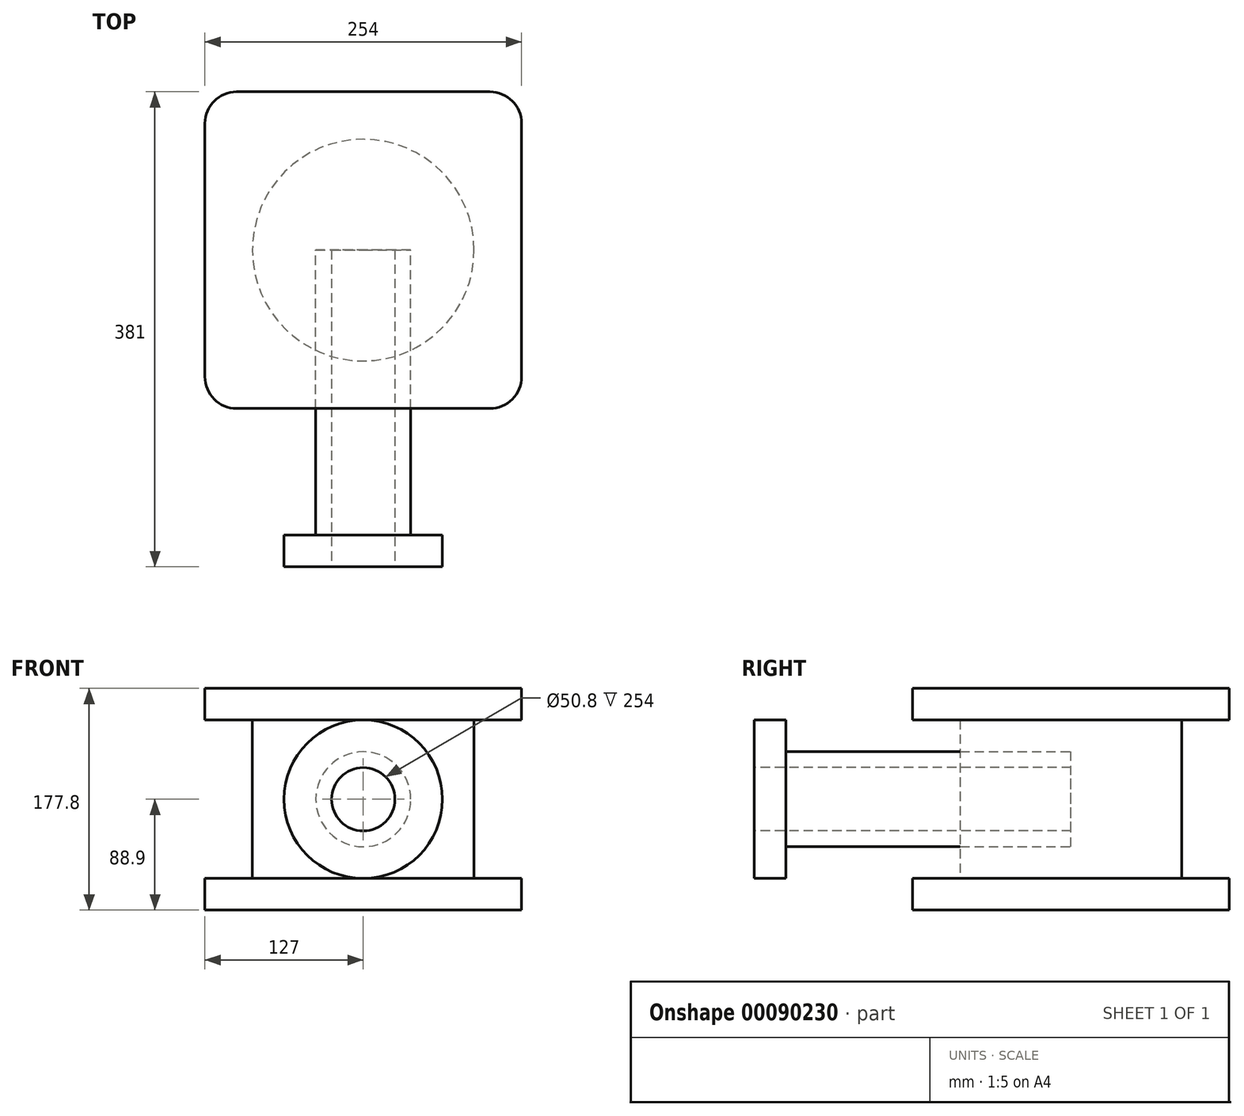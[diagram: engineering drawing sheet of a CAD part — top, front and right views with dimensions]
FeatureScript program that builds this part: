
annotation { "Feature Type Name" : "Feature", "Feature Type Description" : "" }
export const myFeature = defineFeature(function(context is Context, id is Id, definition is map)
    precondition{}
    {
        {
            var Q0;
            Q0=qCreatedBy(makeId("Top.planeOp"),FACE);
            var sketch = newSketch(context, id + "F0", { "sketchPlane" : qUnion([Q0])});
            skLineSegment(sketch, "E0", {"start": v(0, 127) * mm, "end": v(101.6, 127) * mm});
            skLineSegment(sketch, "E1", {"start": v(127, 101.6) * mm, "end": v(127, 0) * mm});
            skLineSegment(sketch, "E2.MirrorCS", {"start": v(0, 127) * mm, "end": v(-101.6, 127) * mm});
            skLineSegment(sketch, "E3.MirrorCS", {"start": v(-127, 101.6) * mm, "end": v(-127, 0) * mm});
            skLineSegment(sketch, "E4.MirrorCS", {"start": v(-127, -101.6) * mm, "end": v(-127, 0) * mm});
            skLineSegment(sketch, "E5.MirrorCS", {"start": v(0, -127) * mm, "end": v(-101.6, -127) * mm});
            skLineSegment(sketch, "E6.MirrorCS", {"start": v(0, -127) * mm, "end": v(101.6, -127) * mm});
            skLineSegment(sketch, "E7.MirrorCS", {"start": v(127, -101.6) * mm, "end": v(127, 0) * mm});
            skPoint(sketch, "E8.visualSharp", {"position": v(-127, 127) * mm});
            skArc(sketch, "E8.filletArc", {"start": v(-101.6, 127) * mm, "mid": v(-119.56, 119.56) * mm, "end": v(-127, 101.6) * mm});
            skPoint(sketch, "E9.visualSharp", {"position": v(127, 127) * mm});
            skArc(sketch, "E9.filletArc", {"start": v(127, 101.6) * mm, "mid": v(119.56, 119.56) * mm, "end": v(101.6, 127) * mm});
            skPoint(sketch, "E10.visualSharp", {"position": v(127, -127) * mm});
            skArc(sketch, "E10.filletArc", {"start": v(101.6, -127) * mm, "mid": v(119.56, -119.56) * mm, "end": v(127, -101.6) * mm});
            skPoint(sketch, "E11.visualSharp", {"position": v(-127, -127) * mm});
            skArc(sketch, "E11.filletArc", {"start": v(-127, -101.6) * mm, "mid": v(-119.56, -119.56) * mm, "end": v(-101.6, -127) * mm});
            skCircle(sketch, "E12", {"center": v(0, 0) * mm, "radius": 88.9 * mm});
            skSolve(sketch);
        }
        {
            var Q0;
            Q0=makeQuery(id+"F0.imprint","IMPRINT",FACE,{"disambiguationData":[TD([[makeQuery(id+"F0.imprint","IMPRINT",EDGE,{"derivedFrom":sQuery(id+"F0.wireOp",EDGE,"E12")}),1.0]])]});
            extrude(context, id + "F1", {"entities" : qUnion([Q0]), "endBound" : BoundingType.SYMMETRIC, "depth" : 127 * mm});
        }
        {
            var Q0;
            Q0=makeQuery(id+"F1.opExtrude","CAP_FACE",FACE,{"disambiguationData":[OSD([sQuery(id+"F0.wireOp",EDGE,"E12")])],"isStart":false});
            var sketch = newSketch(context, id + "F2", { "sketchPlane" : qUnion([Q0])});
            skLineSegment(sketch, "E13", {"start": v(0, 127) * mm, "end": v(101.6, 127) * mm});
            skLineSegment(sketch, "E14", {"start": v(127, 101.6) * mm, "end": v(127, 0) * mm});
            skLineSegment(sketch, "E15.MirrorCS", {"start": v(0, 127) * mm, "end": v(-101.6, 127) * mm});
            skLineSegment(sketch, "E16.MirrorCS", {"start": v(-127, 101.6) * mm, "end": v(-127, 0) * mm});
            skLineSegment(sketch, "E17.MirrorCS", {"start": v(-127, -101.6) * mm, "end": v(-127, 0) * mm});
            skLineSegment(sketch, "E18.MirrorCS", {"start": v(0, -127) * mm, "end": v(-101.6, -127) * mm});
            skLineSegment(sketch, "E19.MirrorCS", {"start": v(0, -127) * mm, "end": v(101.6, -127) * mm});
            skLineSegment(sketch, "E20.MirrorCS", {"start": v(127, -101.6) * mm, "end": v(127, 0) * mm});
            skPoint(sketch, "E21.visualSharp", {"position": v(127, 127) * mm});
            skArc(sketch, "E21.filletArc", {"start": v(127, 101.6) * mm, "mid": v(119.56, 119.56) * mm, "end": v(101.6, 127) * mm});
            skPoint(sketch, "E22.visualSharp", {"position": v(-127, 127) * mm});
            skArc(sketch, "E22.filletArc", {"start": v(-101.6, 127) * mm, "mid": v(-119.56, 119.56) * mm, "end": v(-127, 101.6) * mm});
            skPoint(sketch, "E23.visualSharp", {"position": v(127, -127) * mm});
            skArc(sketch, "E23.filletArc", {"start": v(101.6, -127) * mm, "mid": v(119.56, -119.56) * mm, "end": v(127, -101.6) * mm});
            skPoint(sketch, "E24.visualSharp", {"position": v(-127, -127) * mm});
            skArc(sketch, "E24.filletArc", {"start": v(-127, -101.6) * mm, "mid": v(-119.56, -119.56) * mm, "end": v(-101.6, -127) * mm});
            skSolve(sketch);
        }
        {
            var Q0;
            Q0 = qSketchRegion(id + "F2", true);
            extrude(context, id + "F3", {"entities" : qUnion([Q0]), "operationType" : NewBodyOperationType.ADD, "depth" : 25.4 * mm});
        }
        {
            var Q0;
            Q0=makeQuery(id+"F1.opExtrude","SWEPT_BODY",BODY,{"disambiguationData":[OSD([sQuery(id+"F0.wireOp",EDGE,"E12")])]});
            var Q1;
            Q1=qCreatedBy(makeId("Top.planeOp"),FACE);
            mirror(context, id + "F4", {"operationType" : NewBodyOperationType.ADD, "entities" : qUnion([Q0]), "mirrorPlane" : qUnion([Q1])});
        }
        {
            var Q0;
            Q0=qCreatedBy(makeId("Front.planeOp"),FACE);
            var sketch = newSketch(context, id + "F5", { "sketchPlane" : qUnion([Q0])});
            skCircle(sketch, "E25", {"center": v(0, 0) * mm, "radius": 38.1 * mm});
            skSolve(sketch);
        }
        {
            var Q0;
            Q0 = qSketchRegion(id + "F5", true);
            extrude(context, id + "F6", {"entities" : qUnion([Q0]), "depth" : 228.6 * mm});
        }
        {
            var Q0;
            Q0=makeQuery(id+"F6.opExtrude","CAP_FACE",FACE,{"disambiguationData":[OSD([sQuery(id+"F5.wireOp",EDGE,"E25")])],"isStart":false});
            var sketch = newSketch(context, id + "F7", { "sketchPlane" : qUnion([Q0])});
            skCircle(sketch, "E26", {"center": v(0, 0) * mm, "radius": 63.5 * mm});
            skSolve(sketch);
        }
        {
            var Q0;
            Q0 = qSketchRegion(id + "F7", true);
            extrude(context, id + "F8", {"entities" : qUnion([Q0]), "operationType" : NewBodyOperationType.ADD, "depth" : 25.4 * mm});
        }
        {
            var Q0;
            Q0=makeQuery(id+"F8.opExtrude","CAP_FACE",FACE,{"disambiguationData":[OSD([sQuery(id+"F7.wireOp",EDGE,"E26")])],"isStart":false});
            var sketch = newSketch(context, id + "F9", { "sketchPlane" : qUnion([Q0])});
            skPoint(sketch, "E27", {"position": v(0, 0) * mm});
            skSolve(sketch);
        }
        {
            var Q0;
            Q0=sQuery(id+"F9.wireOp",VERTEX,"E27");
            var Q1;
            Q1=makeQuery(id+"F6.opExtrude","SWEPT_BODY",BODY,{"disambiguationData":[OSD([sQuery(id+"F5.wireOp",EDGE,"E25")])]});
            hole(context, id + "F10", {"style" : HoleStyle.SIMPLE, "endStyle" : HoleEndStyle.THROUGH, "holeDiameter" : 50.8 * mm, "startFromSketch" : true, "locations" : qUnion([Q0]), "scope" : qUnion([Q1]), "isTappedThrough" : true});
        }
    });
